# Revit family: LigULing-Industrial-GEWISS-SMART[4]UL_HIGHBAYS-LED_1M
name_source: partatom
category: Apparecchi per illuminazione
units: mm (PartAtom-declared; Revit-internal decimal feet)

## family parameters
Basato su piano di lavoro = Sì
Condiviso = No
Numero OmniClass = 23.80.00.00
Punto di calcolo locali = No
Quota connettore circolare = Usa diametro
Sempre verticale = No
Sorgente d'illuminazione = No
Taglio con vuoti quando caricato = No
Tipo di parte = Normale
Titolo OmniClass = Electric Power and Lighting

## types (6) — shared parameters
Application = Internal
Body = PA6 "Halogen Free" loaded fibreglass
Carico apparente = 50 VA
Catalogue = LIGHTING
Classification: = -
Classificazione = Lighting
Color Rendering Index = CRI-80
Colour = Grey RAL 7035
Colour : = Grey RAL 7035
Commenti sul wattaggio = 50W
Context = Logistics and industrial manufacturing lighting
Control System = ON / OFF
Control System : = ON / OFF
DIN 18032-3 certification = -
Device with reduced surface temperature = Yes
Distanza tot_plafoniera = 74 mm  [stored 0.242782 ft]
Driver = Included
Driver Box = Built-in
Electrocod = 2444
Eletrical and lighting features = -
External screw = Stainless steel
Fixing = -
Gasket = anti-aging silicone
General information = -
Glow Wire Test : = 850 °C
IDF = 71f814ec-73e0-404d-83ff-d37e06ec48dc
IDT = 510f01894ba548e3aae17db348ab79c9
IP degree = IP66
IPEA = -
Immagine tipo = GWL1071.jpg
Installationa and maintenance = -
Insulation class = I
LED Maintenance = Non-replaceable
Lampada = LED
Larghezza = 253 mm  [stored 0.830052 ft]
Lifetime = L90B10 (Tq+25°C) = 100.000 h - L90B10 (Tq+40°C) = 50.000 h
Locking Hook = -
Luminaire = LED Industrial ReflectorÂ
Lunghezza = 383 mm  [stored 1.25656 ft]
Materials = -
Maximum surface exposed to the wind : = 0,097 m²
Motore = <Per categoria>
Mouting and installation = Ceiling - Wallmounting - Suspension
Operating temperature : = -25°C / +40 °C
Optic Maintenance = Non-replaceable
Optic and illuminating features = -
Overvoltage protection = DM 6 kV / CM 10 kV
Photobiological Risk Class = RG0
Plafoniera = <Per categoria>
Produttore = GEWISS S.p.A.
Prospetto di default = 1219 mm
Raggio led = 30 mm  [stored 0.0984252 ft]
Rated frequency (Hz) = 50/60 Hz
Shield type = Tempered glass Thickness 4mm
Shock resistance = IK08
Spessore plafoniera = 40 mm
Standard Deviation Colour Matching = SDCM = 3
Standard- = UL 1598 - CSA C22.2 No. 250.0-18
Standards and approvals = -
Stocking temperature = -
Supply voltage = 120-277 V
System power = 65W
Technical sheet = https://www.gewiss.com
Tilt- = With bracket accessory
Trasformatore = <Per categoria>
Type of light source = LED - Not replaceable
URL = https://www.gewiss.com
Unique digital code (Datamatrix) = Datamatrix
Version file RFA = 20.11
Vetro acceso = Lampada accesa
Voltaggio = 230 V
Warranty = 5 years
Weight (kg): = 3,5
Wiring = Single wiring with anti-breathing cable exiting metallic PG (NO Connector)

## per-type parameters (varying)
| type | Colour temperature | Descrizione | Efficiency (lm/W) | Lumen output (lm) | Modello | Optic | Optic : | SEO | Unified Glare Rating |
| GWS4120GP840 - SMART4LB 1M ST.AL.ON/OFF UL 90° 40K | 4000K | SMART[4]LB 1M ST.AL.ON/OFF UL 90° 40K | 140 | 9100 | GWS4120GP840 | 90° | Metallic PC reflector and PMMA lenses |  | UGR - 25 |
| GWS4120GH840 - SMART4LB 1M ST.AL.ON/OFF UL 60° 40K | 4000K | SMART[4]LB 1M ST.AL.ON/OFF UL 60° 40K | 138 | 9000 | GWS4120GH840 | 60° | Metallic PC reflector and PMMA lenses |  | UGR - 25 |
| GWS4120GH857 - SMART4LB 1M ST.AL.ON/OFF UL 60° 57K | 5700K | SMART[4]LB 1M ST.AL.ON/OFF UL 60° 57K | 138 | 9000 | GWS4120GH857 | 60° | Metallic PC reflector and PMMA lenses |  | UGR - 25 |
| GWS4120GA857 - SMART4LB 1M ST.AL.ON/OFF UL ARR.57K | 5700K | SMART[4]LB 1M ST.AL.ON/OFF UL ARR.57K | 137 | 8900 | GWS4120GA857 | Array | Metallized polycarbonate reflector | Low bay | - |
| GWS4120GP857 - SMART4LB 1M ST.AL.ON/OFF UL 90° 57K | 5700K | SMART[4]LB 1M ST.AL.ON/OFF UL 90° 57K | 140 | 9100 | GWS4120GP857 | 90° | Metallic PC reflector and PMMA lenses |  | UGR - 25 |
| GWS4120GA840 - SMART4LB 1M ST.AL.ON/OFF UL ARR.40K | 4000K | SMART[4]LB 1M ST.AL.ON/OFF UL ARR.40K | 137 | 8900 | GWS4120GA840 | Array | Metallized polycarbonate reflector | Low bay | - |

note: [stored X ft] marks values corroborated as IEEE doubles in the binary element streams (Revit-internal decimal feet)

## geometry (parser evidence)
native form markers: Blend x4
no freeform markers — native parametric forms only
